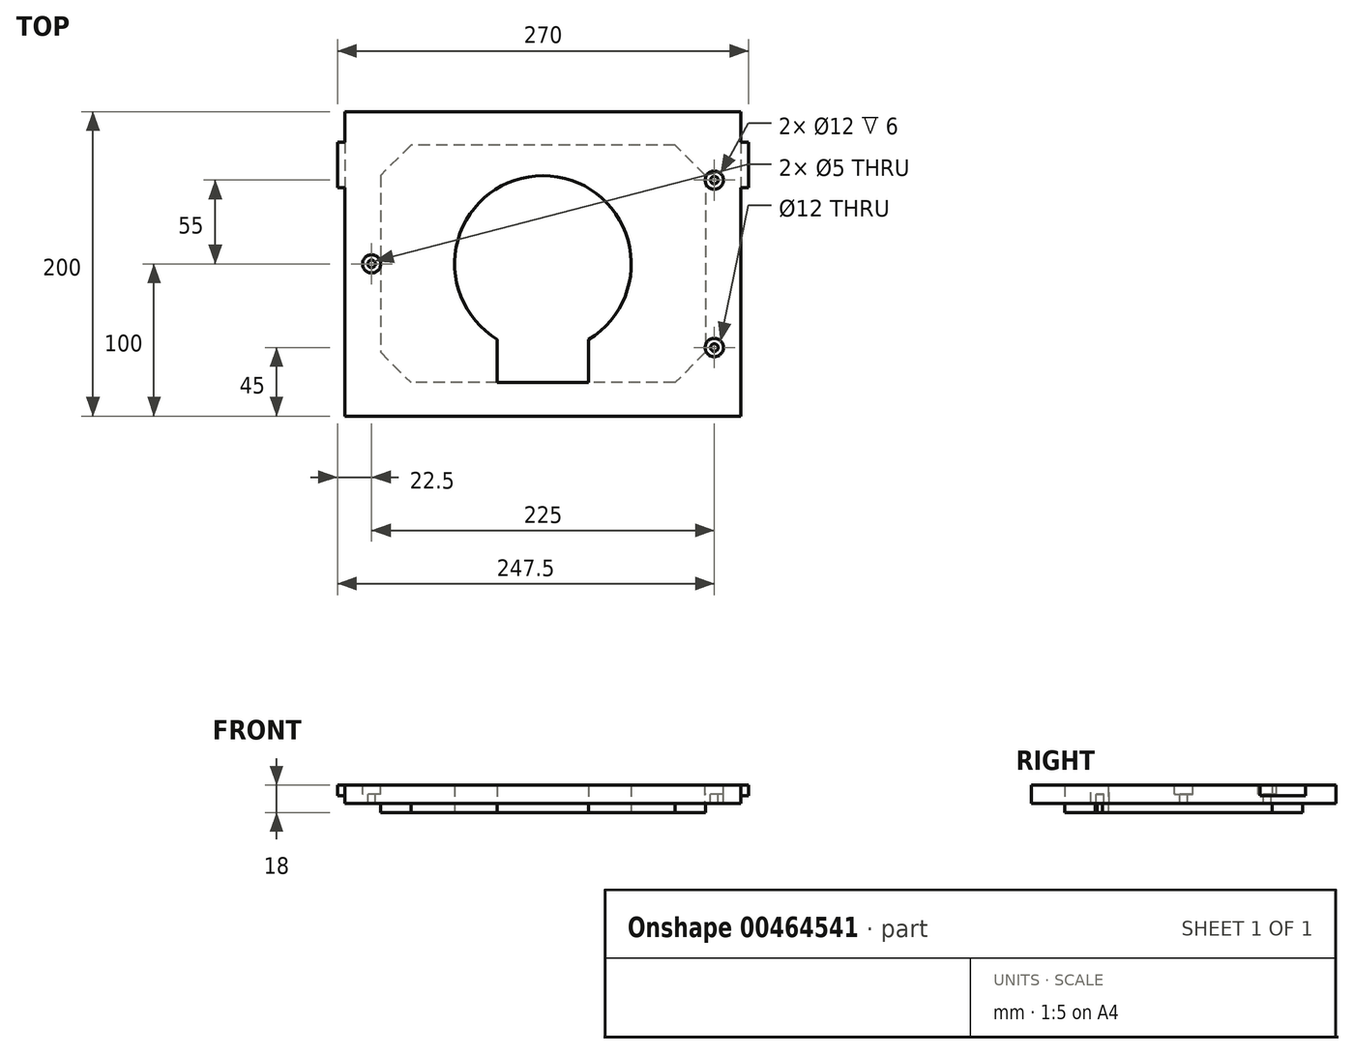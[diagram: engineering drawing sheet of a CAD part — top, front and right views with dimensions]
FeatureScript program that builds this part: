
annotation { "Feature Type Name" : "Feature", "Feature Type Description" : "" }
export const myFeature = defineFeature(function(context is Context, id is Id, definition is map)
    precondition{}
    {
        {
            var Q0;
            Q0=qCreatedBy(makeId("Top.planeOp"),FACE);
            var sketch = newSketch(context, id + "F0", { "sketchPlane" : qUnion([Q0])});
            skLineSegment(sketch, "E0.bottom", {"start": v(86.75, 78) * mm, "end": v(-86.75, 78) * mm});
            skLineSegment(sketch, "E0.top", {"start": v(86.75, -78) * mm, "end": v(30, -78) * mm});
            skLineSegment(sketch, "E0.left", {"start": v(106.75, 58) * mm, "end": v(106.75, -58) * mm});
            skLineSegment(sketch, "E0.right", {"start": v(-106.75, 58) * mm, "end": v(-106.75, -58) * mm});
            skPoint(sketch, "E0.middle", {"position": v(0, 0) * mm});
            skArc(sketch, "E1", {"start": v(30, -49.64) * mm, "mid": v(0, 58) * mm, "end": v(-30, -49.64) * mm});
            skLineSegment(sketch, "E2", {"start": v(-86.75, 78) * mm, "end": v(-106.75, 58) * mm});
            skLineSegment(sketch, "E3", {"start": v(-106.75, -58) * mm, "end": v(-86.75, -78) * mm});
            skLineSegment(sketch, "E4", {"start": v(106.75, -58) * mm, "end": v(86.75, -78) * mm});
            skLineSegment(sketch, "E5", {"start": v(106.75, 58) * mm, "end": v(86.75, 78) * mm});
            skPoint(sketch, "E6.orphan", {"position": v(-106.75, 78) * mm});
            skPoint(sketch, "E7.orphan", {"position": v(-106.75, -78) * mm});
            skPoint(sketch, "E8.orphan", {"position": v(106.75, -78) * mm});
            skPoint(sketch, "E9.orphan", {"position": v(106.75, 78) * mm});
            skPoint(sketch, "E10", {"position": v(-106.75, 0) * mm});
            skPoint(sketch, "E11", {"position": v(0, 78) * mm});
            skPoint(sketch, "E12", {"position": v(106.75, 0) * mm});
            skPoint(sketch, "E13", {"position": v(0, -78) * mm});
            skLineSegment(sketch, "E14", {"start": v(-30, -49.64) * mm, "end": v(-30, -78) * mm});
            skLineSegment(sketch, "E15", {"start": v(30, -49.64) * mm, "end": v(30, -78) * mm});
            skLineSegment(sketch, "E16.trimOffspring", {"start": v(-30, -78) * mm, "end": v(-86.75, -78) * mm});
            skLineSegment(sketch, "E17", {"start": v(-30, -78) * mm, "end": v(30, -78) * mm});
            skLineSegment(sketch, "E18.bottom", {"start": v(130, 100) * mm, "end": v(-130, 100) * mm});
            skLineSegment(sketch, "E18.top", {"start": v(130, -100) * mm, "end": v(-130, -100) * mm});
            skLineSegment(sketch, "E18.left", {"start": v(130, 100) * mm, "end": v(130, -100) * mm});
            skLineSegment(sketch, "E18.right", {"start": v(-130, 100) * mm, "end": v(-130, -100) * mm});
            skSolve(sketch);
        }
        {
            var Q0;
            Q0=makeQuery(id+"F0.imprint","IMPRINT",FACE,{"disambiguationData":[TD([[makeQuery(id+"F0.imprint","IMPRINT",EDGE,{"derivedFrom":sQuery(id+"F0.wireOp",EDGE,"E0.bottom")}),-1.0]])]});
            var Q1;
            Q1=makeQuery(id+"F0.imprint","IMPRINT",FACE,{"disambiguationData":[TD([[makeQuery(id+"F0.imprint","IMPRINT",EDGE,{"derivedFrom":sQuery(id+"F0.wireOp",EDGE,"E0.bottom")}),1.0]])]});
            extrude(context, id + "F1", {"entities" : qUnion([Q0, Q1]), "depth" : 12 * mm});
        }
        {
            var Q0;
            Q0=makeQuery(id+"F0.imprint","IMPRINT",FACE,{"disambiguationData":[TD([[makeQuery(id+"F0.imprint","IMPRINT",EDGE,{"derivedFrom":sQuery(id+"F0.wireOp",EDGE,"E0.bottom")}),1.0]])]});
            extrude(context, id + "F2", {"entities" : qUnion([Q0]), "operationType" : NewBodyOperationType.ADD, "oppositeDirection" : true, "depth" : 6 * mm});
        }
        {
            var Q0;
            Q0=makeQuery(id+"F1.opExtrude","CAP_FACE",FACE,{"disambiguationData":[OSD([sQuery(id+"F0.wireOp",EDGE,"E1"),sQuery(id+"F0.wireOp",EDGE,"E14"),sQuery(id+"F0.wireOp",EDGE,"E15"),sQuery(id+"F0.wireOp",EDGE,"E17"),sQuery(id+"F0.wireOp",EDGE,"E18.bottom"),sQuery(id+"F0.wireOp",EDGE,"E18.top"),sQuery(id+"F0.wireOp",EDGE,"E18.left"),sQuery(id+"F0.wireOp",EDGE,"E18.right")])],"isStart":false});
            var sketch = newSketch(context, id + "F3", { "sketchPlane" : qUnion([Q0])});
            skLineSegment(sketch, "E19.bottom", {"start": v(-130, 80) * mm, "end": v(-135, 80) * mm});
            skLineSegment(sketch, "E19.top", {"start": v(-130, 50) * mm, "end": v(-135, 50) * mm});
            skLineSegment(sketch, "E19.left", {"start": v(-130, 80) * mm, "end": v(-130, 50) * mm});
            skLineSegment(sketch, "E19.right", {"start": v(-135, 80) * mm, "end": v(-135, 50) * mm});
            skLineSegment(sketch, "E20", {"start": v(0, 58) * mm, "end": v(0, -78) * mm, "construction": true});
            skLineSegment(sketch, "E21.MirrorCS", {"start": v(130, 50) * mm, "end": v(135, 50) * mm});
            skLineSegment(sketch, "E22.MirrorCS", {"start": v(130, 80) * mm, "end": v(130, 50) * mm});
            skLineSegment(sketch, "E23.MirrorCS", {"start": v(130, 80) * mm, "end": v(135, 80) * mm});
            skLineSegment(sketch, "E24.MirrorCS", {"start": v(135, 80) * mm, "end": v(135, 50) * mm});
            skSolve(sketch);
        }
        {
            var Q0;
            Q0=makeQuery(id+"F3.imprint","IMPRINT",FACE,{"disambiguationData":[TD([[makeQuery(id+"F3.imprint","IMPRINT",EDGE,{"derivedFrom":sQuery(id+"F3.wireOp",EDGE,"E19.bottom")}),1.0]])]});
            var Q1;
            Q1=makeQuery(id+"F3.imprint","IMPRINT",FACE,{"disambiguationData":[TD([[makeQuery(id+"F3.imprint","IMPRINT",EDGE,{"derivedFrom":sQuery(id+"F3.wireOp",EDGE,"E21.MirrorCS")}),1.0]])]});
            extrude(context, id + "F4", {"entities" : qUnion([Q0, Q1]), "operationType" : NewBodyOperationType.ADD, "oppositeDirection" : true, "depth" : 7 * mm});
        }
        {
            var Q0;
            Q0=makeQuery(id+"F4.boolean.opBoolean","MERGE",FACE,{"derivedFrom":[makeQuery(id+"F1.opExtrude","CAP_FACE",FACE,{"disambiguationData":[OSD([sQuery(id+"F0.wireOp",EDGE,"E1"),sQuery(id+"F0.wireOp",EDGE,"E14"),sQuery(id+"F0.wireOp",EDGE,"E15"),sQuery(id+"F0.wireOp",EDGE,"E17"),sQuery(id+"F0.wireOp",EDGE,"E18.bottom"),sQuery(id+"F0.wireOp",EDGE,"E18.top"),sQuery(id+"F0.wireOp",EDGE,"E18.left"),sQuery(id+"F0.wireOp",EDGE,"E18.right")])],"isStart":false}),makeQuery(id+"F4.opExtrude","CAP_FACE",FACE,{"disambiguationData":[OSD([sQuery(id+"F3.wireOp",EDGE,"E19.bottom"),sQuery(id+"F3.wireOp",EDGE,"E19.top"),sQuery(id+"F3.wireOp",EDGE,"E19.left"),sQuery(id+"F3.wireOp",EDGE,"E19.right")])],"isStart":true}),makeQuery(id+"F4.opExtrude","CAP_FACE",FACE,{"disambiguationData":[OSD([sQuery(id+"F3.wireOp",EDGE,"E21.MirrorCS"),sQuery(id+"F3.wireOp",EDGE,"E22.MirrorCS"),sQuery(id+"F3.wireOp",EDGE,"E23.MirrorCS"),sQuery(id+"F3.wireOp",EDGE,"E24.MirrorCS")])],"isStart":true})]});
            var sketch = newSketch(context, id + "F5", { "sketchPlane" : qUnion([Q0])});
            skLineSegment(sketch, "E25", {"start": v(0, 100) * mm, "end": v(0, -100) * mm, "construction": true});
            skLineSegment(sketch, "E26", {"start": v(130, 0) * mm, "end": v(-130, 0) * mm, "construction": true});
            skCircle(sketch, "E27", {"center": v(-112.5, 0) * mm, "radius": 2.5 * mm});
            skCircle(sketch, "E28", {"center": v(112.5, 55) * mm, "radius": 2.5 * mm});
            skLineSegment(sketch, "E29", {"start": v(112.5, 100) * mm, "end": v(112.5, -100) * mm, "construction": true});
            skCircle(sketch, "E30.MirrorC", {"center": v(112.5, -55) * mm, "radius": 2.5 * mm});
            skCircle(sketch, "E31", {"center": v(-112.5, 0) * mm, "radius": 6 * mm});
            skCircle(sketch, "E32", {"center": v(112.5, 55) * mm, "radius": 6 * mm});
            skCircle(sketch, "E33.MirrorC", {"center": v(112.5, -55) * mm, "radius": 6 * mm});
            skSolve(sketch);
        }
        {
            var Q0;
            Q0=makeQuery(id+"F5.imprint","IMPRINT",FACE,{"disambiguationData":[TD([[makeQuery(id+"F5.imprint","IMPRINT",EDGE,{"derivedFrom":sQuery(id+"F5.wireOp",EDGE,"E27")}),-1.0]])]});
            var Q1;
            Q1=makeQuery(id+"F5.imprint","IMPRINT",FACE,{"disambiguationData":[TD([[makeQuery(id+"F5.imprint","IMPRINT",EDGE,{"derivedFrom":sQuery(id+"F5.wireOp",EDGE,"E27")}),1.0]])]});
            var Q2;
            Q2=makeQuery(id+"F5.imprint","IMPRINT",FACE,{"disambiguationData":[TD([[makeQuery(id+"F5.imprint","IMPRINT",EDGE,{"derivedFrom":sQuery(id+"F5.wireOp",EDGE,"E28")}),-1.0]])]});
            var Q3;
            Q3=makeQuery(id+"F5.imprint","IMPRINT",FACE,{"disambiguationData":[TD([[makeQuery(id+"F5.imprint","IMPRINT",EDGE,{"derivedFrom":sQuery(id+"F5.wireOp",EDGE,"E28")}),1.0]])]});
            var Q4;
            Q4=makeQuery(id+"F5.imprint","IMPRINT",FACE,{"disambiguationData":[TD([[makeQuery(id+"F5.imprint","IMPRINT",EDGE,{"derivedFrom":sQuery(id+"F5.wireOp",EDGE,"E30.MirrorC")}),-1.0]])]});
            var Q5;
            Q5=makeQuery(id+"F5.imprint","IMPRINT",FACE,{"disambiguationData":[TD([[makeQuery(id+"F5.imprint","IMPRINT",EDGE,{"derivedFrom":sQuery(id+"F5.wireOp",EDGE,"E30.MirrorC")}),1.0]])]});
            extrude(context, id + "F6", {"entities" : qUnion([Q0, Q1, Q2, Q3, Q4, Q5]), "operationType" : NewBodyOperationType.REMOVE, "oppositeDirection" : true, "depth" : 6 * mm});
        }
        {
            var Q0;
            Q0=makeQuery(id+"F5.imprint","IMPRINT",FACE,{"disambiguationData":[TD([[makeQuery(id+"F5.imprint","IMPRINT",EDGE,{"derivedFrom":sQuery(id+"F5.wireOp",EDGE,"E27")}),1.0]])]});
            var Q1;
            Q1=makeQuery(id+"F5.imprint","IMPRINT",FACE,{"disambiguationData":[TD([[makeQuery(id+"F5.imprint","IMPRINT",EDGE,{"derivedFrom":sQuery(id+"F5.wireOp",EDGE,"E28")}),1.0]])]});
            var Q2;
            Q2=makeQuery(id+"F5.imprint","IMPRINT",FACE,{"disambiguationData":[TD([[makeQuery(id+"F5.imprint","IMPRINT",EDGE,{"derivedFrom":sQuery(id+"F5.wireOp",EDGE,"E30.MirrorC")}),-1.0]])]});
            extrude(context, id + "F7", {"entities" : qUnion([Q0, Q1, Q2]), "operationType" : NewBodyOperationType.REMOVE, "endBound" : BoundingType.THROUGH_ALL, "oppositeDirection" : true, "depth" : 25 * mm});
        }
    });
